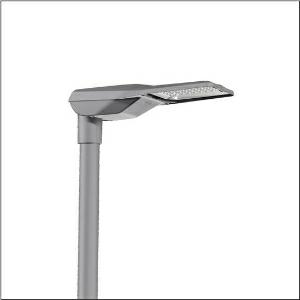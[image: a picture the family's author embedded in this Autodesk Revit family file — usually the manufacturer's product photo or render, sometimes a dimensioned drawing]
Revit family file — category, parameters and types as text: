
# Revit family: streetlight_sl_21_iq_mini___st1_5a_5xe2p41g08hb_3230
name_source: partatom
category: Lighting Fixtures
units: mm (PartAtom-declared; Revit-internal decimal feet)

## family parameters
Cut with Voids When Loaded = No
Host = Face
Light Source = No
Part Type = Normal
Room Calculation Point = No
Round Connector Dimension = Use Diameter
Shared = No

## types (1)
- --- (1 x LED, 9690 lm, 70.9 W, 4000K)
    Apparent Load = 71 VA
    CIE Flux Codes = 22 53 95 100 100
    Color Rendering = 70
    Color Temperature = 4000K
    Default Elevation = 1800 mm
    Description = Streetlight SL 21 iQ mini, mast luminaire, primary light control with lens, of PMMA, primary optical cover: cover, of toughened safety glass, transparent, light distribution: ST1.5a, light emission: direct distribution, primary light characteristic: asymmetric, installation type: post-top, side-entry, LED, High Power LED, rated luminous flux: 9.690lm, luminous efficacy: 137lm/W, light colour: 740, colour temperature: 4000K, control gear: iQ Street-Remote, control: Street-Remote, Auto-Match, Temp-Guard, Lumen-Switch, Night-Set, Smart-Wire, Light-Fading, Desk-Remote (wireless, voltage-free reading and setting of iQ features in the workshop via application-optimized NFC function/RFID function), optimised constant luminous flux control (CLO 2.0), pre-setting: linear dimming characteristic, mains connection: 220..240V, AC, 50/60Hz, start of lifetime: 71W, end of service life: 75W, reduction: 31W, luminaire housing, of diecast aluminium, powder-coated, Siteco® metallic grey (DB 702S), corrosivity category C5 mid according to DIN EN ISO 12944, please order mast flange separately, inclination adjustable: 0°, 5°, 10°, 15°, sealing non-destructively replaceable, multi-level sealing system, length: 628mm, width: 235mm, height: 110mm, mast flange for spigot size: 42mm (side-entry): 5XC10008XM4, 60/48mm (side-entry/post-top): 5XC10108XM2, 76/60mm (side-entry/post-top): 5XC10108XM1, mounting height: 4..8m, protection rating (complete): IP66, insulation class (complete): insulation class II (safety insulation), certification: CE, ENEC, ENEC+, VDE, impact resistance: IK10, permissible operating ambient temperature for outdoor applications: -40..+50°C, standard-compliant lighting for roads and squares, packaging unit: 1 piece

Light Distribution: ST1.5a
    Height = 110 mm
    Lamp = 1 x LED
    Lamp Light Flux = 9690 lm
    Lamp Power = 70.9 W
    Lamp count = 1
    Length = 625 mm
    Luminous efficacy = 137 lm/W
    Manufacturer = Siteco
    ModVariant = No
    Model = 5XE2P41G08HB
    Number of Poles = 1
    OnlyDefault = Yes
    Power Factor = 1
    Product Name = Streetlight SL 21 iQ mini | ST1.5a
    Product group = mast luminaire | pylon top
    ProductGroupID = 6100
    Protection Class = Protection class II
    Protection Degree = IP 66
    RLX_Detail_Level = 1
    RLX_Emergency_Light_Flux = 0 lm
    RLX_Emergency_Type = 0
    RLX_Emergency_Type_DB = No
    RlxData = <blob elided: 29861 chars, md5=a68d76c3>
    Socket = socket
    Standby Power = 0 W
    System Light Flux = 9690 lm
    System Power = 71 W
    Type Comments = factory setting: luminous flux: 100 % | dim-lin: 254 | 711 mA
    Type Image = l_1003519.jpg
    URL = http://relux.com
    VarID = @adj_157010
    Voltage = 0 V
    Weight = 0.00 kg
    Width = 234 mm

## geometry (parser evidence)
native form markers: Blend x4, Sweep x11
no freeform markers — native parametric forms only
